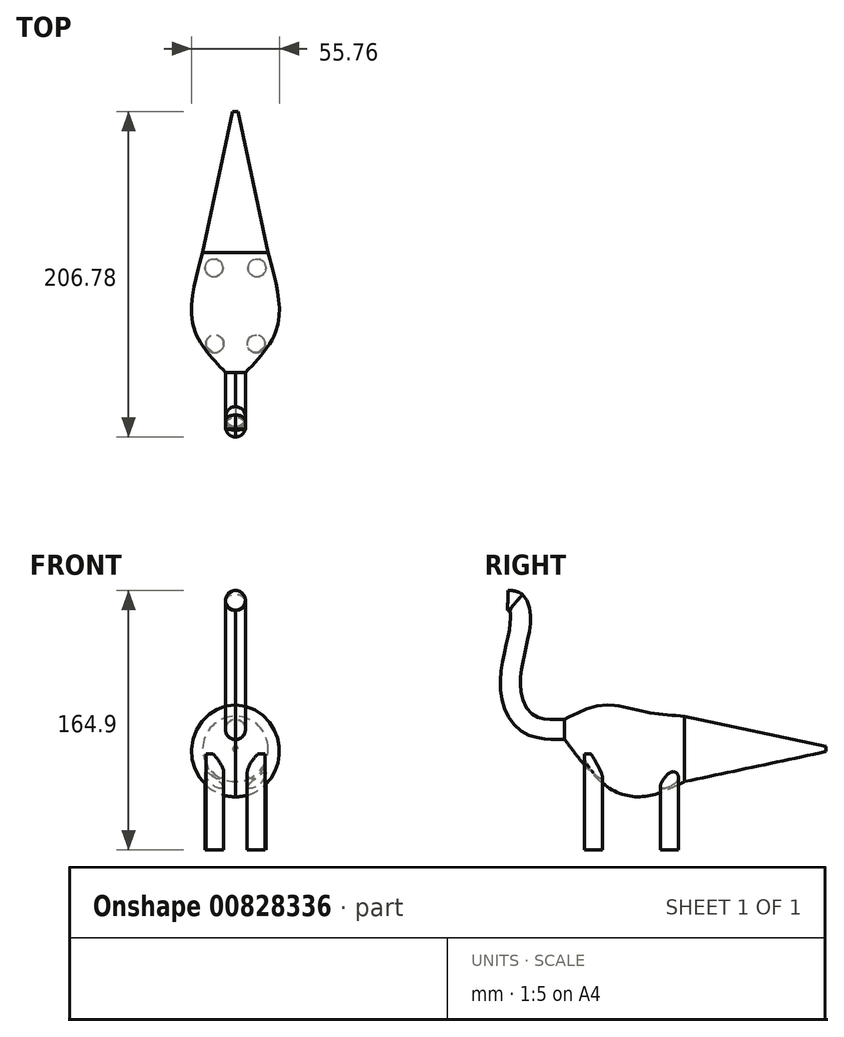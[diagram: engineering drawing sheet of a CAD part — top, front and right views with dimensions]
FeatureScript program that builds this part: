
annotation { "Feature Type Name" : "Feature", "Feature Type Description" : "" }
export const myFeature = defineFeature(function(context is Context, id is Id, definition is map)
    precondition{}
    {
        {
            var Q0;
            Q0=qCreatedBy(makeId("Front.planeOp"),FACE);
            var sketch = newSketch(context, id + "F0", { "sketchPlane" : qUnion([Q0])});
            skCircle(sketch, "E0", {"center": v(0, 0) * mm, "radius": 26.87 * mm});
            skSolve(sketch);
        }
        {
            var Q0;
            Q0=qCreatedBy(makeId("Front.planeOp"),FACE);
            cPlane(context, id + "F1", {"entities" : qUnion([Q0]), "cplaneType" : CPlaneType.OFFSET, "offset" : 25.4 * mm, "width" : 152.4 * mm, "height" : 152.4 * mm});
        }
        {
            var Q0;
            Q0=qCreatedBy(makeId("Front.planeOp"),FACE);
            cPlane(context, id + "F2", {"entities" : qUnion([Q0]), "cplaneType" : CPlaneType.OFFSET, "offset" : 25.4 * mm, "oppositeDirection" : true, "width" : 152.4 * mm, "height" : 152.4 * mm});
        }
        {
            var Q0;
            Q0=qCreatedBy(id+"F1.planeOp",FACE);
            var sketch = newSketch(context, id + "F3", { "sketchPlane" : qUnion([Q0])});
            skCircle(sketch, "E1", {"center": v(0, 5.8) * mm, "radius": 25.4 * mm});
            skSolve(sketch);
        }
        {
            var Q0;
            Q0=qCreatedBy(id+"F2.planeOp",FACE);
            var sketch = newSketch(context, id + "F4", { "sketchPlane" : qUnion([Q0])});
            skCircle(sketch, "E2", {"center": v(0, 3.31) * mm, "radius": 20.79 * mm});
            skSolve(sketch);
        }
        {
            var Q0;
            Q0=qCreatedBy(id+"F1.planeOp",FACE);
            cPlane(context, id + "F5", {"entities" : qUnion([Q0]), "cplaneType" : CPlaneType.OFFSET, "offset" : 25.4 * mm, "width" : 152.4 * mm, "height" : 152.4 * mm});
        }
        {
            var Q0;
            Q0=qCreatedBy(id+"F5.planeOp",FACE);
            var sketch = newSketch(context, id + "F6", { "sketchPlane" : qUnion([Q0])});
            skCircle(sketch, "E3", {"center": v(0, 15.7) * mm, "radius": 6.35 * mm});
            skSolve(sketch);
        }
        {
            var Q0;
            Q0=qCreatedBy(makeId("Right.planeOp"),FACE);
            var sketch = newSketch(context, id + "F7", { "sketchPlane" : qUnion([Q0])});
            skPoint(sketch, "E4.0", {"position": v(-50.8, 15.7) * mm});
            skFitSpline(sketch, "E5", {"points": [v(-50.8, 15.7) * mm, v(-58.38, 15.7) * mm, v(-74.38, 19.64) * mm, v(-85.1, 39.86) * mm, v(-81.58, 69.05) * mm, v(-78.9, 89.12) * mm, v(-82.04, 96.66) * mm, v(-86.91, 97.6) * mm], "startDerivative": vector(-63.05, -2.64) * mm, "endDerivative": vector(-62.5, -0.44) * mm});
            skSolve(sketch);
        }
        {
            var Q0;
            Q0=makeQuery(id+"F4.imprint","IMPRINT",FACE,{"disambiguationData":[TD([[makeQuery(id+"F4.imprint","IMPRINT",EDGE,{"derivedFrom":sQuery(id+"F4.wireOp",EDGE,"E2")}),1.0]])]});
            var Q1;
            Q1=makeQuery(id+"F0.imprint","IMPRINT",FACE,{"disambiguationData":[TD([[makeQuery(id+"F0.imprint","IMPRINT",EDGE,{"derivedFrom":sQuery(id+"F0.wireOp",EDGE,"E0")}),1.0]])]});
            var Q2;
            Q2=makeQuery(id+"F3.imprint","IMPRINT",FACE,{"disambiguationData":[TD([[makeQuery(id+"F3.imprint","IMPRINT",EDGE,{"derivedFrom":sQuery(id+"F3.wireOp",EDGE,"E1")}),1.0]])]});
            var Q3;
            Q3=makeQuery(id+"F6.imprint","IMPRINT",FACE,{"disambiguationData":[TD([[makeQuery(id+"F6.imprint","IMPRINT",EDGE,{"derivedFrom":sQuery(id+"F6.wireOp",EDGE,"E3")}),1.0]])]});
            loft(context, id + "F8", {"sheetProfilesArray" : [{ "sheetProfileEntities" : qUnion([Q0]) }, { "sheetProfileEntities" : qUnion([Q1]) }, { "sheetProfileEntities" : qUnion([Q2]) }, { "sheetProfileEntities" : qUnion([Q3]) }]});
        }
        {
            var Q0;
            Q0=makeQuery(id+"F8.opLoft","CAP_FACE",FACE,{"disambiguationData":[OSD([makeQuery(id+"F6.imprint","IMPRINT",FACE,{"disambiguationData":[TD([[makeQuery(id+"F6.imprint","IMPRINT",EDGE,{"derivedFrom":sQuery(id+"F6.wireOp",EDGE,"E3")}),1.0]])]})])],"isStart":true});
            var Q1;
            Q1=sQuery(id+"F7.wireOp",EDGE,"E5");
            sweep(context, id + "F9", {"profiles" : qUnion([Q0]), "path" : qUnion([Q1])});
        }
        {
            var Q0;
            Q0=makeQuery(id+"F8.opLoft","CAP_FACE",FACE,{"disambiguationData":[OSD([makeQuery(id+"F4.imprint","IMPRINT",FACE,{"disambiguationData":[TD([[makeQuery(id+"F4.imprint","IMPRINT",EDGE,{"derivedFrom":sQuery(id+"F4.wireOp",EDGE,"E2")}),1.0]])]})])],"isStart":true});
            extrude(context, id + "F10", {"entities" : qUnion([Q0]), "depth" : 89.66 * mm, "offsetDistance" : 25.4 * mm, "hasDraft" : true, "draftAngle" : 12 * degree, "draftPullDirection" : true});
        }
        {
            var Q0;
            Q0=qCreatedBy(makeId("Top.planeOp"),FACE);
            var sketch = newSketch(context, id + "F11", { "sketchPlane" : qUnion([Q0])});
            skCircle(sketch, "E6", {"center": v(13.14, -32.55) * mm, "radius": 5.67 * mm});
            skCircle(sketch, "E7", {"center": v(13.64, 15.75) * mm, "radius": 5.67 * mm});
            skCircle(sketch, "E8.MirrorC", {"center": v(-13.14, -32.55) * mm, "radius": 5.67 * mm});
            skCircle(sketch, "E9.MirrorC", {"center": v(-13.64, 15.75) * mm, "radius": 5.67 * mm});
            skSolve(sketch);
        }
        {
            var Q0;
            Q0 = qSketchRegion(id + "F11", true);
            extrude(context, id + "F12", {"entities" : qUnion([Q0]), "operationType" : NewBodyOperationType.ADD, "oppositeDirection" : true, "depth" : 60.96 * mm, "offsetDistance" : 25.4 * mm});
        }
    });
